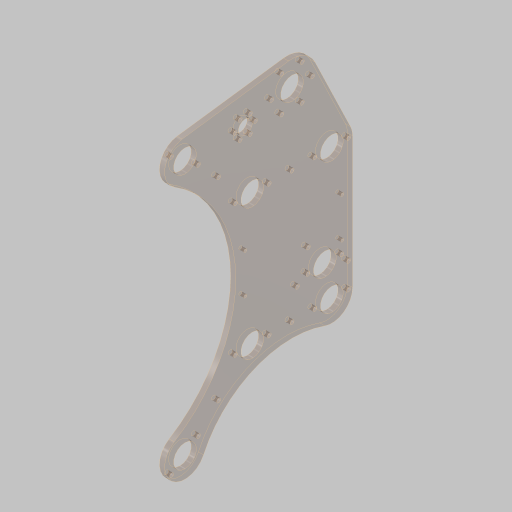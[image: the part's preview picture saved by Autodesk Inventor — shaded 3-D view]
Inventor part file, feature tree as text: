
AUTODESK INVENTOR PART (.ipt)
format: ipt  version: 2023.5 (Build 275446000, 446)  size: 476,672 bytes
history: native  units: in
note: dims shown in document units (in); Inventor stores cm internally (conversion verified against a paired STEP export)
features: sketch x6, hole x5, projected_geometry x2, extrude x1
ambient origin geometry x8: Origin, YZ Plane, XZ Plane, XY Plane, X Axis, Y Axis, Z Axis, Center Point
bodies: Solid1 (feature_tree)
feature tree (14):
  sketch  "Sketch1"  dims[d0=1.0in d1=2.0in]
  sketch  "Sketch2"  dims[d2=3.0in d4=3.8976in]
  extrude  "Extrusion1"  Depth=1.0in
  hole  "Hole1"  [1 undecoded]
  hole  "Hole2"  [1 undecoded]
  hole  "Hole3"  [1 undecoded]
  hole  "Hole4"  [1 undecoded]
  hole  "Hole5"  [1 undecoded]
  sketch  "Sketch3"  dims[d5=3.6869in d6=12.0in]
  sketch  "Sketch4"  dims[d7=0.125in d8=0.125in]
  projected_geometry  "Projected Loop1"
  sketch  "Sketch5"  dims[d9=5.0in d10=15.0in]
  sketch  "Sketch6"  dims[d11=2.0in d12=2.0in d13=4.4882in d14=11.0in d15=1.115in d16=1.5in d17=3.095in d18=2.0in d19=0.25in d31=1.655in d32=0.375in d33=0.25in d34=0.0in d35=1.9488in d36=1.5in d37=1.0in d38=0.69in d50=0.5in d51=0.5in d52=0.201in d53=0.75in d54=0.385in d55=0.25in d56=0.5635in d57=1.0in d58=0.8108in d59=2.3622in d61=360.0deg d63=2.9551in d64=3.0in d68=4.25in d69=1.0in d70=3.0in d71=2.5in d72=3.2185in d73=6.4369in d74=4.7835in d75=1.7in d77=2.0in d78=2.3622in d80=360.0deg d82=0.201in d83=0.75in d84=0.385in d85=0.25in d86=0.5635in d87=1.0in d88=0.8108in d89=0.201in d90=0.328in d91=0.385in d92=0.25in d93=0.5635in d94=1.0in d95=0.8108in d97=1.5in d98=2.517in d99=2.517in d101=0.481in d102=1.25in d104=0.201in d105=0.75in d106=0.375in d107=0.25in d108=0.5635in d109=1.0in d110=0.8108in d111=0.375in d112=0.375in d113=0.375in d114=1.9366in d115=0.5in d116=1.9366in d117=4.75in d118=0.15in d119=0.75in d120=0.279in d121=0.25in d122=0.5635in d123=1.0in d124=0.8108in]
  projected_geometry  "Project Cut Edges1"
note: 5 required parameter values undecoded (feature->parameter linkage not recoverable at this tier; creation-order binding heuristic only, values carry confidence <= 0.55)
